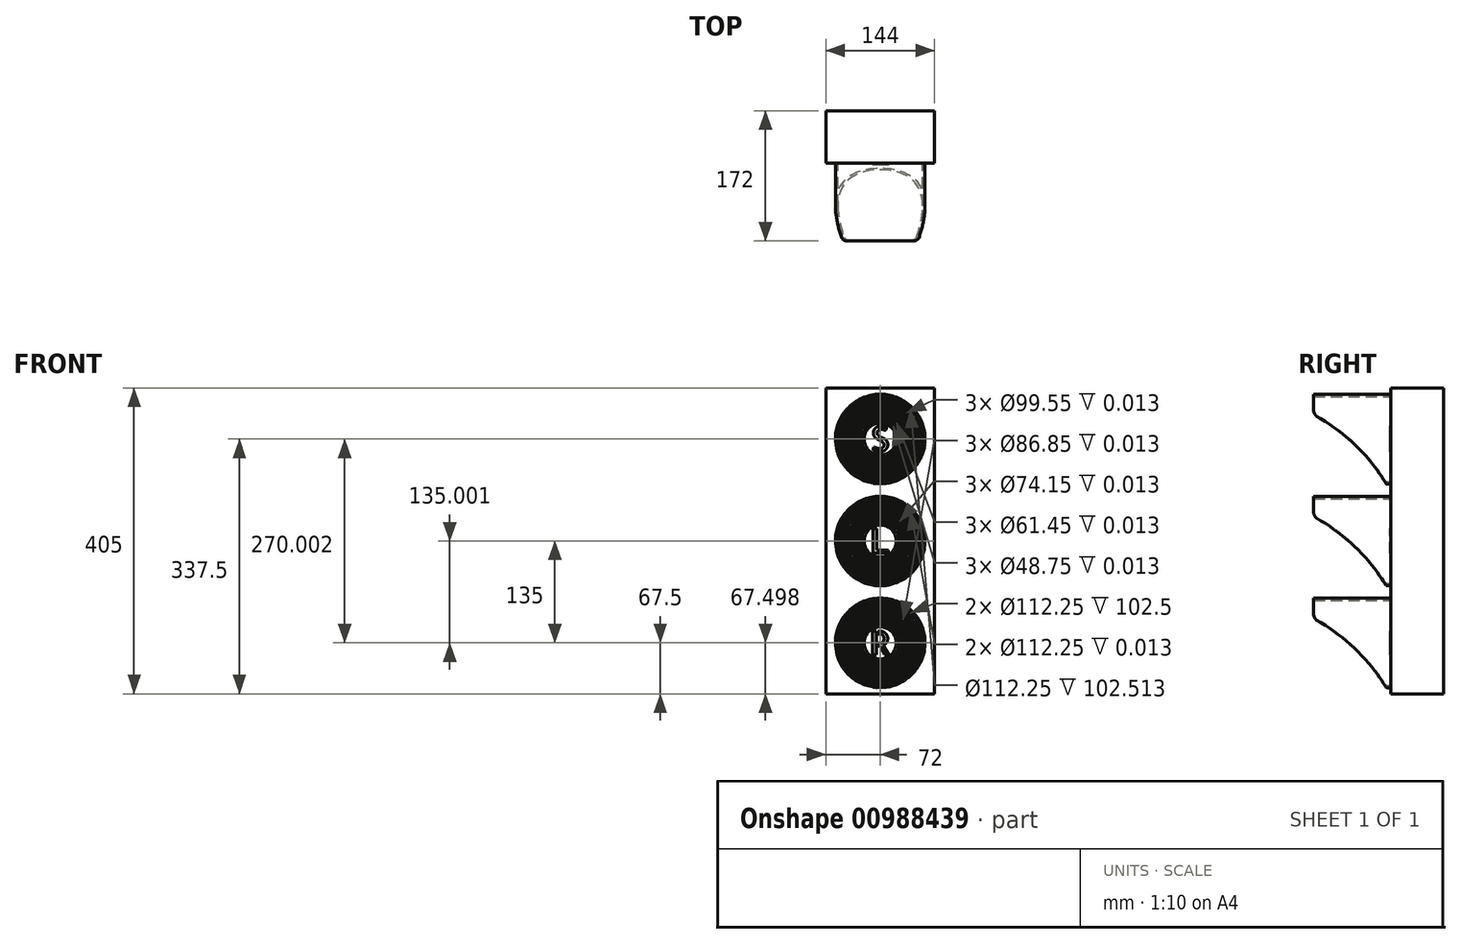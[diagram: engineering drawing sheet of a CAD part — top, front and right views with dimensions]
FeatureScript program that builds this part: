
annotation { "Feature Type Name" : "Feature", "Feature Type Description" : "" }
export const myFeature = defineFeature(function(context is Context, id is Id, definition is map)
    precondition{}
    {
        {
            var Q0;
            Q0=qCreatedBy(makeId("Front.planeOp"),FACE);
            var sketch = newSketch(context, id + "F0", { "sketchPlane" : qUnion([Q0])});
            skLineSegment(sketch, "E0.bottom", {"start": v(144, 405) * mm, "end": v(-144, 405) * mm});
            skLineSegment(sketch, "E0.top", {"start": v(144, -405) * mm, "end": v(-144, -405) * mm});
            skLineSegment(sketch, "E0.left", {"start": v(144, 405) * mm, "end": v(144, -405) * mm});
            skLineSegment(sketch, "E0.right", {"start": v(-144, 405) * mm, "end": v(-144, -405) * mm});
            skPoint(sketch, "E0.middle", {"position": v(0, 0) * mm});
            skSolve(sketch);
        }
        {
            var Q0;
            Q0 = qSketchRegion(id + "F0", true);
            extrude(context, id + "F1", {"entities" : qUnion([Q0]), "depth" : 139 * mm, "offsetDistance" : 25.4 * mm, "symmetric" : true});
        }
        {
            var Q0;
            Q0=makeQuery(id+"F1.opExtrude","CAP_FACE",FACE,{"disambiguationData":[OSD([sQuery(id+"F0.wireOp",EDGE,"E0.bottom"),sQuery(id+"F0.wireOp",EDGE,"E0.top"),sQuery(id+"F0.wireOp",EDGE,"E0.left"),sQuery(id+"F0.wireOp",EDGE,"E0.right")])],"isStart":false});
            var sketch = newSketch(context, id + "F2", { "sketchPlane" : qUnion([Q0])});
            skLineSegment(sketch, "E1", {"start": v(-144, 0) * mm, "end": v(144, 0) * mm, "construction": true});
            skLineSegment(sketch, "E2", {"start": v(0, 405) * mm, "end": v(0, 135) * mm, "construction": true});
            skLineSegment(sketch, "E3", {"start": v(0, 135) * mm, "end": v(0, -135) * mm, "construction": true});
            skLineSegment(sketch, "E4", {"start": v(0, -135) * mm, "end": v(0, -405) * mm, "construction": true});
            skCircle(sketch, "E5", {"center": v(0, 270) * mm, "radius": 118.6 * mm});
            skCircle(sketch, "E6", {"center": v(0, 0) * mm, "radius": 118.6 * mm});
            skCircle(sketch, "E7", {"center": v(0, -270) * mm, "radius": 118.6 * mm});
            skLineSegment(sketch, "E8", {"start": v(0, -270) * mm, "end": v(-118.6, -270) * mm, "construction": true});
            skLineSegment(sketch, "E9", {"start": v(-118.6, -270) * mm, "end": v(-144, -270) * mm, "construction": true});
            skCircle(sketch, "E10.0", {"center": v(0, 270) * mm, "radius": 112.25 * mm});
            skCircle(sketch, "E11.0", {"center": v(0, 0) * mm, "radius": 112.25 * mm});
            skCircle(sketch, "E12.0", {"center": v(0, -270) * mm, "radius": 112.25 * mm});
            skSolve(sketch);
        }
        {
            var Q0;
            Q0=makeQuery(id+"F2.imprint","IMPRINT",FACE,{"disambiguationData":[TD([[makeQuery(id+"F2.imprint","IMPRINT",EDGE,{"derivedFrom":sQuery(id+"F2.wireOp",EDGE,"E5")}),1.0]])]});
            var Q1;
            Q1=makeQuery(id+"F2.imprint","IMPRINT",FACE,{"disambiguationData":[TD([[makeQuery(id+"F2.imprint","IMPRINT",EDGE,{"derivedFrom":sQuery(id+"F2.wireOp",EDGE,"E6")}),1.0]])]});
            var Q2;
            Q2=makeQuery(id+"F2.imprint","IMPRINT",FACE,{"disambiguationData":[TD([[makeQuery(id+"F2.imprint","IMPRINT",EDGE,{"derivedFrom":sQuery(id+"F2.wireOp",EDGE,"E7")}),1.0]])]});
            extrude(context, id + "F3", {"entities" : qUnion([Q0, Q1, Q2]), "operationType" : NewBodyOperationType.ADD, "depth" : 205 * mm, "offsetDistance" : 25.4 * mm});
        }
        {
            var Q0;
            Q0=qCreatedBy(makeId("Right.planeOp"),FACE);
            var sketch = newSketch(context, id + "F4", { "sketchPlane" : qUnion([Q0])});
            skLineSegment(sketch, "E13", {"start": v(-266.78, 330.32) * mm, "end": v(-82.2, 151.4) * mm, "construction": true});
            skLineSegment(sketch, "E14", {"start": v(-69.5, 151.4) * mm, "end": v(-82.2, 151.4) * mm, "construction": true});
            skLineSegment(sketch, "E15", {"start": v(-274.5, 388.6) * mm, "end": v(-69.5, 388.6) * mm, "construction": true});
            skLineSegment(sketch, "E16", {"start": v(-274.5, 388.6) * mm, "end": v(-274.5, 348.55) * mm, "construction": true});
            skPoint(sketch, "E17.visualSharp", {"position": v(-274.5, 337.8) * mm});
            skArc(sketch, "E17.filletArc", {"start": v(-274.5, 348.55) * mm, "mid": v(-272.5, 338.65) * mm, "end": v(-266.78, 330.32) * mm});
            skArc(sketch, "E18", {"start": v(-82.2, 151.4) * mm, "mid": v(-162.99, 252.73) * mm, "end": v(-266.78, 330.32) * mm});
            skLineSegment(sketch, "E19", {"start": v(-274.5, 348.55) * mm, "end": v(-274.5, 151.4) * mm});
            skLineSegment(sketch, "E20", {"start": v(-82.2, 151.4) * mm, "end": v(-274.5, 151.4) * mm});
            skArc(sketch, "E21.0.1.0", {"start": v(-82.2, -118.6) * mm, "mid": v(-162.99, -17.28) * mm, "end": v(-266.78, 60.31) * mm});
            skArc(sketch, "E21.0.1.1", {"start": v(-274.5, 78.55) * mm, "mid": v(-272.5, 68.65) * mm, "end": v(-266.78, 60.31) * mm});
            skLineSegment(sketch, "E21.0.1.2", {"start": v(-274.5, 78.55) * mm, "end": v(-274.5, -118.6) * mm});
            skLineSegment(sketch, "E21.0.1.3", {"start": v(-82.2, -118.6) * mm, "end": v(-274.5, -118.6) * mm});
            skArc(sketch, "E21.0.2.0", {"start": v(-82.2, -388.6) * mm, "mid": v(-162.99, -287.28) * mm, "end": v(-266.78, -209.69) * mm});
            skArc(sketch, "E21.0.2.1", {"start": v(-274.5, -191.45) * mm, "mid": v(-272.5, -201.35) * mm, "end": v(-266.78, -209.69) * mm});
            skLineSegment(sketch, "E21.0.2.2", {"start": v(-274.5, -191.45) * mm, "end": v(-274.5, -388.6) * mm});
            skLineSegment(sketch, "E21.0.2.3", {"start": v(-82.2, -388.6) * mm, "end": v(-274.5, -388.6) * mm});
            skLineSegment(sketch, "E21.direction1", {"start": v(-516.56, -112.04) * mm, "end": v(-491.16, -112.04) * mm, "construction": true});
            skLineSegment(sketch, "E21.direction2", {"start": v(-516.56, -112.04) * mm, "end": v(-516.56, -382.04) * mm, "construction": true});
            skSolve(sketch);
        }
        {
            var Q0;
            Q0 = qSketchRegion(id + "F4", true);
            extrude(context, id + "F5", {"entities" : qUnion([Q0]), "operationType" : NewBodyOperationType.REMOVE, "endBound" : BoundingType.THROUGH_ALL, "oppositeDirection" : true, "depth" : 25.4 * mm, "offsetDistance" : 25.4 * mm, "hasSecondDirection" : true, "secondDirectionBound" : BoundingType.THROUGH_ALL, "secondDirectionOppositeDirection" : false, "secondDirectionDepth" : 25.4 * mm});
        }
        {
            var Q0;
            Q0=makeQuery(id+"F3.boolean.opBoolean","SPLIT",FACE,{"disambiguationData":[TD([makeQuery(id+"F3.opExtrude","SWEPT_FACE",FACE,{"disambiguationData":[OSD([sQuery(id+"F2.wireOp",EDGE,"E10.0")])]})])],"derivedFrom":makeQuery(id+"F1.opExtrude","CAP_FACE",FACE,{"disambiguationData":[OSD([sQuery(id+"F0.wireOp",EDGE,"E0.bottom"),sQuery(id+"F0.wireOp",EDGE,"E0.top"),sQuery(id+"F0.wireOp",EDGE,"E0.left"),sQuery(id+"F0.wireOp",EDGE,"E0.right")])],"isStart":false})});
            var sketch = newSketch(context, id + "F6", { "sketchPlane" : qUnion([Q0])});
            skCircle(sketch, "E22.0", {"center": v(0, 270) * mm, "radius": 112.25 * mm});
            skCircle(sketch, "E23.0", {"center": v(0, 270) * mm, "radius": 105.9 * mm});
            skCircle(sketch, "E24.0", {"center": v(0, 270) * mm, "radius": 99.55 * mm});
            skCircle(sketch, "E25.0", {"center": v(0, 270) * mm, "radius": 93.2 * mm});
            skCircle(sketch, "E26.0", {"center": v(0, 270) * mm, "radius": 86.85 * mm});
            skCircle(sketch, "E27.0", {"center": v(0, 270) * mm, "radius": 80.5 * mm});
            skCircle(sketch, "E28.0", {"center": v(0, 270) * mm, "radius": 74.15 * mm});
            skCircle(sketch, "E29.0", {"center": v(0, 270) * mm, "radius": 67.8 * mm});
            skCircle(sketch, "E30.0", {"center": v(0, 270) * mm, "radius": 61.45 * mm});
            skCircle(sketch, "E31.0", {"center": v(0, 270) * mm, "radius": 55.1 * mm});
            skCircle(sketch, "E32.0", {"center": v(0, 270) * mm, "radius": 48.75 * mm});
            skCircle(sketch, "E33.0", {"center": v(0, 270) * mm, "radius": 42.4 * mm});
            skCircle(sketch, "E34.0.1.0", {"center": v(0, 0) * mm, "radius": 112.25 * mm});
            skCircle(sketch, "E34.0.1.1", {"center": v(0, 0) * mm, "radius": 105.9 * mm});
            skCircle(sketch, "E34.0.1.2", {"center": v(0, 0) * mm, "radius": 99.55 * mm});
            skCircle(sketch, "E34.0.1.3", {"center": v(0, 0) * mm, "radius": 93.2 * mm});
            skCircle(sketch, "E34.0.1.4", {"center": v(0, 0) * mm, "radius": 86.85 * mm});
            skCircle(sketch, "E34.0.1.5", {"center": v(0, 0) * mm, "radius": 80.5 * mm});
            skCircle(sketch, "E34.0.1.6", {"center": v(0, 0) * mm, "radius": 74.15 * mm});
            skCircle(sketch, "E34.0.1.7", {"center": v(0, 0) * mm, "radius": 67.8 * mm});
            skCircle(sketch, "E34.0.1.8", {"center": v(0, 0) * mm, "radius": 61.45 * mm});
            skCircle(sketch, "E34.0.1.9", {"center": v(0, 0) * mm, "radius": 55.1 * mm});
            skCircle(sketch, "E34.0.1.10", {"center": v(0, 0) * mm, "radius": 48.75 * mm});
            skCircle(sketch, "E34.0.1.11", {"center": v(0, 0) * mm, "radius": 42.4 * mm});
            skCircle(sketch, "E34.0.2.0", {"center": v(0, -270) * mm, "radius": 112.25 * mm});
            skCircle(sketch, "E34.0.2.1", {"center": v(0, -270) * mm, "radius": 105.9 * mm});
            skCircle(sketch, "E34.0.2.2", {"center": v(0, -270) * mm, "radius": 99.55 * mm});
            skCircle(sketch, "E34.0.2.3", {"center": v(0, -270) * mm, "radius": 93.2 * mm});
            skCircle(sketch, "E34.0.2.4", {"center": v(0, -270) * mm, "radius": 86.85 * mm});
            skCircle(sketch, "E34.0.2.5", {"center": v(0, -270) * mm, "radius": 80.5 * mm});
            skCircle(sketch, "E34.0.2.6", {"center": v(0, -270) * mm, "radius": 74.15 * mm});
            skCircle(sketch, "E34.0.2.7", {"center": v(0, -270) * mm, "radius": 67.8 * mm});
            skCircle(sketch, "E34.0.2.8", {"center": v(0, -270) * mm, "radius": 61.45 * mm});
            skCircle(sketch, "E34.0.2.9", {"center": v(0, -270) * mm, "radius": 55.1 * mm});
            skCircle(sketch, "E34.0.2.10", {"center": v(0, -270) * mm, "radius": 48.75 * mm});
            skCircle(sketch, "E34.0.2.11", {"center": v(0, -270) * mm, "radius": 42.4 * mm});
            skLineSegment(sketch, "E34.direction1", {"start": v(0, 270) * mm, "end": v(25.4, 270) * mm, "construction": true});
            skLineSegment(sketch, "E34.direction2", {"start": v(0, 270) * mm, "end": v(0, 0) * mm, "construction": true});
            skSolve(sketch);
        }
        {
            var Q0;
            Q0=makeQuery(id+"F6.imprint","IMPRINT",FACE,{"disambiguationData":[TD([[makeQuery(id+"F6.imprint","IMPRINT",EDGE,{"derivedFrom":sQuery(id+"F6.wireOp",EDGE,"E22.0")}),1.0]])]});
            var Q1;
            Q1=makeQuery(id+"F6.imprint","IMPRINT",FACE,{"disambiguationData":[TD([[makeQuery(id+"F6.imprint","IMPRINT",EDGE,{"derivedFrom":sQuery(id+"F6.wireOp",EDGE,"E24.0")}),1.0]])]});
            var Q2;
            Q2=makeQuery(id+"F6.imprint","IMPRINT",FACE,{"disambiguationData":[TD([[makeQuery(id+"F6.imprint","IMPRINT",EDGE,{"derivedFrom":sQuery(id+"F6.wireOp",EDGE,"E26.0")}),1.0]])]});
            var Q3;
            Q3=makeQuery(id+"F6.imprint","IMPRINT",FACE,{"disambiguationData":[TD([[makeQuery(id+"F6.imprint","IMPRINT",EDGE,{"derivedFrom":sQuery(id+"F6.wireOp",EDGE,"E28.0")}),1.0]])]});
            var Q4;
            Q4=makeQuery(id+"F6.imprint","IMPRINT",FACE,{"disambiguationData":[TD([[makeQuery(id+"F6.imprint","IMPRINT",EDGE,{"derivedFrom":sQuery(id+"F6.wireOp",EDGE,"E30.0")}),1.0]])]});
            var Q5;
            Q5=makeQuery(id+"F6.imprint","IMPRINT",FACE,{"disambiguationData":[TD([[makeQuery(id+"F6.imprint","IMPRINT",EDGE,{"derivedFrom":sQuery(id+"F6.wireOp",EDGE,"E32.0")}),1.0]])]});
            var Q6;
            Q6=makeQuery(id+"F6.imprint","IMPRINT",FACE,{"disambiguationData":[TD([[makeQuery(id+"F6.imprint","IMPRINT",EDGE,{"derivedFrom":sQuery(id+"F6.wireOp",EDGE,"E34.0.1.0")}),1.0]])]});
            var Q7;
            Q7=makeQuery(id+"F6.imprint","IMPRINT",FACE,{"disambiguationData":[TD([[makeQuery(id+"F6.imprint","IMPRINT",EDGE,{"derivedFrom":sQuery(id+"F6.wireOp",EDGE,"E34.0.1.2")}),1.0]])]});
            var Q8;
            Q8=makeQuery(id+"F6.imprint","IMPRINT",FACE,{"disambiguationData":[TD([[makeQuery(id+"F6.imprint","IMPRINT",EDGE,{"derivedFrom":sQuery(id+"F6.wireOp",EDGE,"E34.0.1.4")}),1.0]])]});
            var Q9;
            Q9=makeQuery(id+"F6.imprint","IMPRINT",FACE,{"disambiguationData":[TD([[makeQuery(id+"F6.imprint","IMPRINT",EDGE,{"derivedFrom":sQuery(id+"F6.wireOp",EDGE,"E34.0.1.6")}),1.0]])]});
            var Q10;
            Q10=makeQuery(id+"F6.imprint","IMPRINT",FACE,{"disambiguationData":[TD([[makeQuery(id+"F6.imprint","IMPRINT",EDGE,{"derivedFrom":sQuery(id+"F6.wireOp",EDGE,"E34.0.1.8")}),1.0]])]});
            var Q11;
            Q11=makeQuery(id+"F6.imprint","IMPRINT",FACE,{"disambiguationData":[TD([[makeQuery(id+"F6.imprint","IMPRINT",EDGE,{"derivedFrom":sQuery(id+"F6.wireOp",EDGE,"E34.0.1.10")}),1.0]])]});
            var Q12;
            Q12=makeQuery(id+"F6.imprint","IMPRINT",FACE,{"disambiguationData":[TD([[makeQuery(id+"F6.imprint","IMPRINT",EDGE,{"derivedFrom":sQuery(id+"F6.wireOp",EDGE,"E34.0.2.0")}),1.0]])]});
            var Q13;
            Q13=makeQuery(id+"F6.imprint","IMPRINT",FACE,{"disambiguationData":[TD([[makeQuery(id+"F6.imprint","IMPRINT",EDGE,{"derivedFrom":sQuery(id+"F6.wireOp",EDGE,"E34.0.2.2")}),1.0]])]});
            var Q14;
            Q14=makeQuery(id+"F6.imprint","IMPRINT",FACE,{"disambiguationData":[TD([[makeQuery(id+"F6.imprint","IMPRINT",EDGE,{"derivedFrom":sQuery(id+"F6.wireOp",EDGE,"E34.0.2.4")}),1.0]])]});
            var Q15;
            Q15=makeQuery(id+"F6.imprint","IMPRINT",FACE,{"disambiguationData":[TD([[makeQuery(id+"F6.imprint","IMPRINT",EDGE,{"derivedFrom":sQuery(id+"F6.wireOp",EDGE,"E34.0.2.6")}),1.0]])]});
            var Q16;
            Q16=makeQuery(id+"F6.imprint","IMPRINT",FACE,{"disambiguationData":[TD([[makeQuery(id+"F6.imprint","IMPRINT",EDGE,{"derivedFrom":sQuery(id+"F6.wireOp",EDGE,"E34.0.2.8")}),1.0]])]});
            var Q17;
            Q17=makeQuery(id+"F6.imprint","IMPRINT",FACE,{"disambiguationData":[TD([[makeQuery(id+"F6.imprint","IMPRINT",EDGE,{"derivedFrom":sQuery(id+"F6.wireOp",EDGE,"E34.0.2.10")}),1.0]])]});
            extrude(context, id + "F7", {"entities" : qUnion([Q0, Q1, Q2, Q3, Q4, Q5, Q6, Q7, Q8, Q9, Q10, Q11, Q12, Q13, Q14, Q15, Q16, Q17]), "operationType" : NewBodyOperationType.REMOVE, "oppositeDirection" : true, "depth" : 0.03 * mm, "offsetDistance" : 25.4 * mm});
        }
        {
            var Q0;
            Q0=makeQuery(id+"F7.boolean.opBoolean","SPLIT",FACE,{"disambiguationData":[TD([makeQuery(id+"F7.opExtrude","SWEPT_FACE",FACE,{"disambiguationData":[OSD([sQuery(id+"F6.wireOp",EDGE,"E33.0")])]})])],"derivedFrom":makeQuery(id+"F3.boolean.opBoolean","SPLIT",FACE,{"disambiguationData":[TD([makeQuery(id+"F3.opExtrude","SWEPT_FACE",FACE,{"disambiguationData":[OSD([sQuery(id+"F2.wireOp",EDGE,"E10.0")])]})])],"derivedFrom":makeQuery(id+"F1.opExtrude","CAP_FACE",FACE,{"disambiguationData":[OSD([sQuery(id+"F0.wireOp",EDGE,"E0.bottom"),sQuery(id+"F0.wireOp",EDGE,"E0.top"),sQuery(id+"F0.wireOp",EDGE,"E0.left"),sQuery(id+"F0.wireOp",EDGE,"E0.right")])],"isStart":false})})});
            var sketch = newSketch(context, id + "F8", { "sketchPlane" : qUnion([Q0])});
            skLineSegment(sketch, "E35", {"start": v(0, 270) * mm, "end": v(0, 312.4) * mm, "construction": true});
            skLineSegment(sketch, "E36", {"start": v(0, 270) * mm, "end": v(0, 227.6) * mm, "construction": true});
            skPoint(sketch, "E37.middle", {"position": v(0, 270) * mm});
            skText(sketch, "E38", { "text": "S", "fontName": "AllertaStencil-Regular.ttf"});
            skLineSegment(sketch, "E39", {"start": v(0, 0) * mm, "end": v(0, 42.4) * mm, "construction": true});
            skText(sketch, "E40", { "text": "L", "fontName": "AllertaStencil-Regular.ttf"});
            skLineSegment(sketch, "E41", {"start": v(0, -270) * mm, "end": v(0, -227.6) * mm, "construction": true});
            skText(sketch, "E42", { "text": "R", "fontName": "AllertaStencil-Regular.ttf"});
            const initialGuessF8  = {"E38": [-0.02614, 0.23662, 1, 0, 0.06676], "E40": [-0.02735, -0.0324, 1, 0, 0.0648], "E42": [-0.02825, -0.30163, 1, 0, 0.06324]};
            skSetInitialGuess(sketch, initialGuessF8);
            skSolve(sketch);
        }
        {
            var Q0;
            Q0=makeQuery(id+"F8.imprint","IMPRINT",FACE,{"disambiguationData":[TD([[makeQuery(id+"F8.imprint","IMPRINT",EDGE,{"derivedFrom":sQuery(id+"F8.wireOp",EDGE,"E40.sketch_text.stroke-0")}),-1.0]])]});
            var Q1;
            Q1=makeQuery(id+"F8.imprint","IMPRINT",FACE,{"disambiguationData":[TD([[makeQuery(id+"F8.imprint","IMPRINT",EDGE,{"derivedFrom":sQuery(id+"F8.wireOp",EDGE,"E42.sketch_text.stroke-0")}),-1.0]])]});
            var Q2;
            Q2=makeQuery(id+"F8.imprint","IMPRINT",FACE,{"disambiguationData":[TD([[makeQuery(id+"F8.imprint","IMPRINT",EDGE,{"derivedFrom":sQuery(id+"F8.wireOp",EDGE,"E42.sketch_text.stroke-4")}),-1.0]])]});
            var Q3;
            Q3=makeQuery(id+"F8.imprint","IMPRINT",FACE,{"disambiguationData":[TD([[makeQuery(id+"F8.imprint","IMPRINT",EDGE,{"derivedFrom":sQuery(id+"F8.wireOp",EDGE,"E38.sketch_text.stroke-0")}),-1.0]])]});
            var Q4;
            Q4=makeQuery(id+"F8.imprint","IMPRINT",FACE,{"disambiguationData":[TD([[makeQuery(id+"F8.imprint","IMPRINT",EDGE,{"derivedFrom":sQuery(id+"F8.wireOp",EDGE,"E38.sketch_text.stroke-25")}),-1.0]])]});
            var Q5;
            Q5=makeQuery(id+"F8.imprint","IMPRINT",FACE,{"disambiguationData":[TD([[makeQuery(id+"F8.imprint","IMPRINT",EDGE,{"derivedFrom":sQuery(id+"F8.wireOp",EDGE,"E38.sketch_text.stroke-37")}),-1.0]])]});
            var Q6;
            Q6=makeQuery(id+"F8.imprint","IMPRINT",FACE,{"disambiguationData":[TD([[makeQuery(id+"F8.imprint","IMPRINT",EDGE,{"derivedFrom":sQuery(id+"F8.wireOp",EDGE,"E38.sketch_text.stroke-11")}),-1.0]])]});
            extrude(context, id + "F9", {"entities" : qUnion([Q0, Q1, Q2, Q3, Q4, Q5, Q6]), "operationType" : NewBodyOperationType.ADD, "depth" : 3.17 * mm, "offsetDistance" : 25.4 * mm});
        }
        {
            var Q0;
            Q0=makeQuery(id+"F1.opExtrude","SWEPT_BODY",BODY,{"disambiguationData":[OSD([sQuery(id+"F0.wireOp",EDGE,"E0.bottom"),sQuery(id+"F0.wireOp",EDGE,"E0.top"),sQuery(id+"F0.wireOp",EDGE,"E0.left"),sQuery(id+"F0.wireOp",EDGE,"E0.right")])]});
            var Q1;
            Q1=makeQuery(id+"F1.opExtrude","CAP_VERTEX",VERTEX,{"disambiguationData":[OSD([sQuery(id+"F0.wireOp",EDGE,"E0.bottom"),sQuery(id+"F0.wireOp",EDGE,"E0.left")])],"isStart":true});
            transform(context, id + "F10", {"entities" : qUnion([Q0]), "transformType" : TransformType.SCALE_UNIFORMLY, "scale" : 0.5, "scalePoint" : qUnion([Q1]), "makeCopy" : false});
        }
    });
